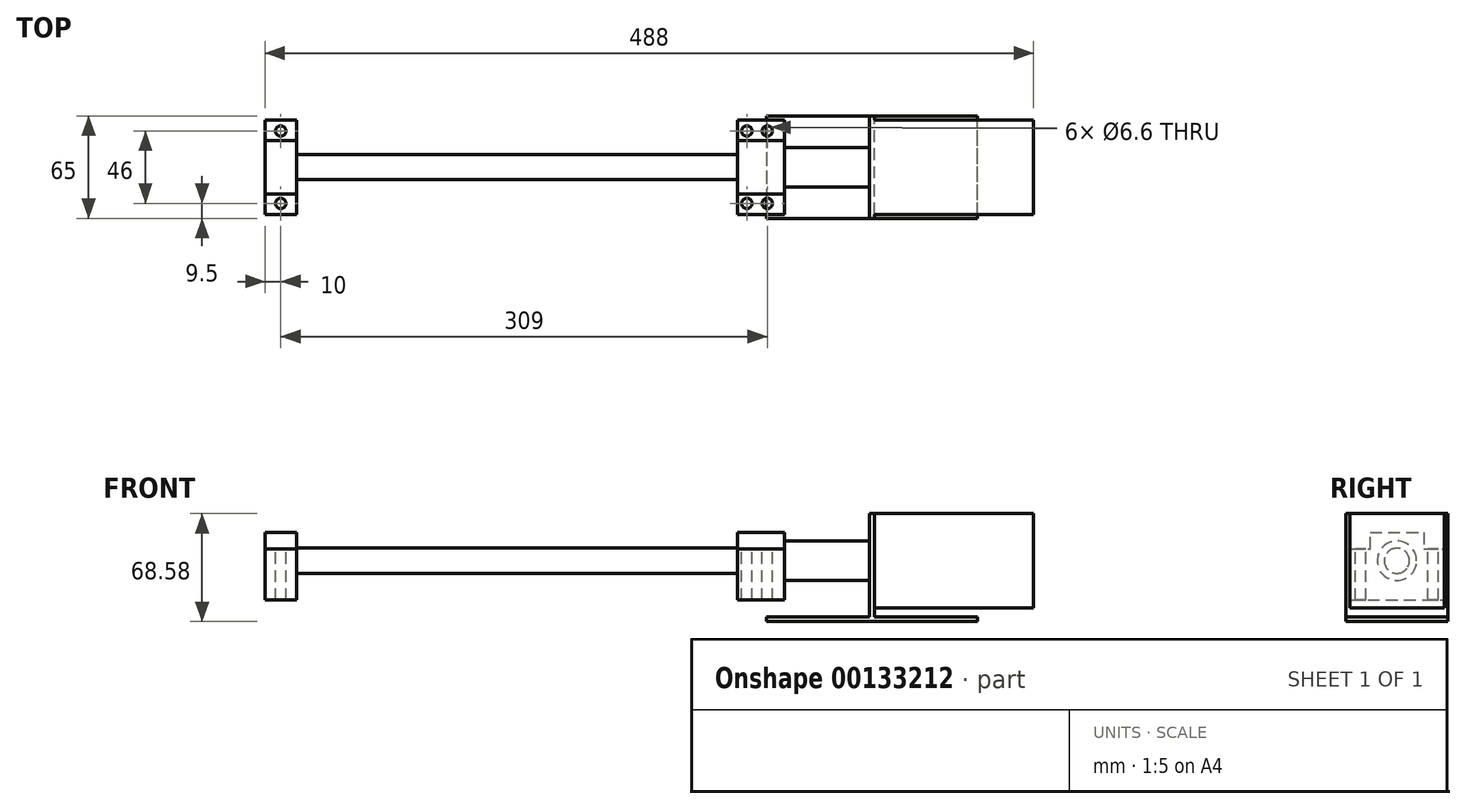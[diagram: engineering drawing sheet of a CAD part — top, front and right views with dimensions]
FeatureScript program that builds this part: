
annotation { "Feature Type Name" : "Feature", "Feature Type Description" : "" }
export const myFeature = defineFeature(function(context is Context, id is Id, definition is map)
    precondition{}
    {
        {
            var Q0;
            Q0=qCreatedBy(makeId("Right.planeOp"),FACE);
            var sketch = newSketch(context, id + "F0", { "sketchPlane" : qUnion([Q0])});
            skCircle(sketch, "E0", {"center": v(0, 0) * mm, "radius": 8 * mm});
            skSolve(sketch);
        }
        {
            var Q0;
            Q0=qSketchRegion(id+"F0",true);
            var Q1;
            Q1=qSketchRegion(id+"F2",true);
            extrude(context, id + "F1", {"entities" : qUnion([Q0, Q1]), "depth" : 330 * mm, "offsetDistance" : 25 * mm});
        }
        {
            var Q0;
            Q0=makeQuery(id+"F1.opExtrude","CAP_FACE",FACE,{"disambiguationData":[OSD([sQuery(id+"F0.wireOp",EDGE,"E0")])],"isStart":false});
            var sketch = newSketch(context, id + "F2", { "sketchPlane" : qUnion([Q0])});
            skLineSegment(sketch, "E1.bottom", {"start": v(17, 7.5) * mm, "end": v(30, 7.5) * mm});
            skLineSegment(sketch, "E1.top", {"start": v(-30, -25) * mm, "end": v(30, -25) * mm});
            skLineSegment(sketch, "E1.left", {"start": v(-30, 7.5) * mm, "end": v(-30, -25) * mm});
            skLineSegment(sketch, "E1.right", {"start": v(30, 7.5) * mm, "end": v(30, -25) * mm});
            skLineSegment(sketch, "E2", {"start": v(-17, 7.5) * mm, "end": v(-17, 18) * mm});
            skLineSegment(sketch, "E3", {"start": v(-17, 18) * mm, "end": v(17, 18) * mm});
            skLineSegment(sketch, "E4", {"start": v(17, 18) * mm, "end": v(17, 7.5) * mm});
            skLineSegment(sketch, "E5", {"start": v(-30, 7.5) * mm, "end": v(-17, 7.5) * mm});
            skSolve(sketch);
        }
        {
            var Q0;
            Q0=qSketchRegion(id+"F2",true);
            extrude(context, id + "F3", {"entities" : qUnion([Q0]), "operationType" : NewBodyOperationType.ADD, "oppositeDirection" : true, "depth" : (30) * mm, "offsetDistance" : 25 * mm});
        }
        {
            var Q0;
            Q0=makeQuery(id+"F1.opExtrude","CAP_FACE",FACE,{"disambiguationData":[OSD([sQuery(id+"F0.wireOp",EDGE,"E0")])],"isStart":true});
            var sketch = newSketch(context, id + "F4", { "sketchPlane" : qUnion([Q0])});
            skLineSegment(sketch, "E6.0", {"start": v(17, 18) * mm, "end": v(-17, 18) * mm});
            skLineSegment(sketch, "E7.0", {"start": v(-17, 18) * mm, "end": v(-17, 7.5) * mm});
            skLineSegment(sketch, "E8.0", {"start": v(-30, 7.5) * mm, "end": v(-30, -25) * mm});
            skLineSegment(sketch, "E9.0", {"start": v(30, -25) * mm, "end": v(-30, -25) * mm});
            skLineSegment(sketch, "E10.0", {"start": v(30, 7.5) * mm, "end": v(30, -25) * mm});
            skLineSegment(sketch, "E11.0", {"start": v(30, 7.5) * mm, "end": v(17, 7.5) * mm});
            skLineSegment(sketch, "E12.0", {"start": v(17, 7.5) * mm, "end": v(17, 18) * mm});
            skLineSegment(sketch, "E13", {"start": v(-30, 7.5) * mm, "end": v(-17, 7.5) * mm});
            skSolve(sketch);
        }
        {
            var Q0;
            Q0=qSketchRegion(id+"F4",true);
            extrude(context, id + "F5", {"entities" : qUnion([Q0]), "operationType" : NewBodyOperationType.ADD, "oppositeDirection" : true, "depth" : (20) * mm, "offsetDistance" : 25 * mm});
        }
        {
            var Q0;
            Q0=makeQuery(id+"F3.boolean.opBoolean","MERGE",FACE,{"derivedFrom":[makeQuery(id+"F1.opExtrude","CAP_FACE",FACE,{"disambiguationData":[OSD([sQuery(id+"F0.wireOp",EDGE,"E0")])],"isStart":false}),makeQuery(id+"F3.opExtrude","CAP_FACE",FACE,{"disambiguationData":[OSD([sQuery(id+"F2.wireOp",EDGE,"E1.bottom"),sQuery(id+"F2.wireOp",EDGE,"E1.top"),sQuery(id+"F2.wireOp",EDGE,"E1.left"),sQuery(id+"F2.wireOp",EDGE,"E1.right"),sQuery(id+"F2.wireOp",EDGE,"E2"),sQuery(id+"F2.wireOp",EDGE,"E3"),sQuery(id+"F2.wireOp",EDGE,"E4"),sQuery(id+"F2.wireOp",EDGE,"E5")])],"isStart":true})]});
            var sketch = newSketch(context, id + "F6", { "sketchPlane" : qUnion([Q0])});
            skCircle(sketch, "E14", {"center": v(0, 0) * mm, "radius": 12.5 * mm});
            skSolve(sketch);
        }
        {
            var Q0;
            Q0=qSketchRegion(id+"F6",true);
            extrude(context, id + "F7", {"entities" : qUnion([Q0]), "operationType" : NewBodyOperationType.ADD, "depth" : (57) * mm, "offsetDistance" : 25 * mm});
        }
        {
            var Q0;
            Q0=makeQuery(id+"F3.opExtrude","SWEPT_FACE",FACE,{"disambiguationData":[OSD([sQuery(id+"F2.wireOp",EDGE,"E3")])]});
            var sketch = newSketch(context, id + "F8", { "sketchPlane" : qUnion([Q0])});
            skCircle(sketch, "E15", {"center": v(306, 23) * mm, "radius": 3.3 * mm});
            skCircle(sketch, "E16", {"center": v(319, 23) * mm, "radius": 3.3 * mm});
            skCircle(sketch, "E17", {"center": v(306, -23) * mm, "radius": 3.3 * mm});
            skCircle(sketch, "E18", {"center": v(319, -23) * mm, "radius": 3.3 * mm});
            skCircle(sketch, "E19", {"center": v(10, 23) * mm, "radius": 3.3 * mm});
            skCircle(sketch, "E20", {"center": v(10, -23) * mm, "radius": 3.3 * mm});
            skSolve(sketch);
        }
        {
            var Q0;
            Q0=qSketchRegion(id+"F8",true);
            extrude(context, id + "F9", {"entities" : qUnion([Q0]), "operationType" : NewBodyOperationType.REMOVE, "endBound" : BoundingType.THROUGH_ALL, "oppositeDirection" : true, "depth" : 25 * mm, "offsetDistance" : 25 * mm});
        }
        {
            var Q0;
            Q0=makeQuery(id+"F7.opExtrude","CAP_FACE",FACE,{"disambiguationData":[OSD([sQuery(id+"F6.wireOp",EDGE,"E14")])],"isStart":false});
            var sketch = newSketch(context, id + "F10", { "sketchPlane" : qUnion([Q0])});
            skLineSegment(sketch, "E21.bottom", {"start": v(-30, 30) * mm, "end": v(30, 30) * mm});
            skLineSegment(sketch, "E21.top", {"start": v(-30, -30) * mm, "end": v(30, -30) * mm});
            skLineSegment(sketch, "E21.left", {"start": v(-30, 30) * mm, "end": v(-30, -30) * mm});
            skLineSegment(sketch, "E21.right", {"start": v(30, 30) * mm, "end": v(30, -30) * mm});
            skSolve(sketch);
        }
        {
            var Q0;
            Q0=qSketchRegion(id+"F10",true);
            extrude(context, id + "F11", {"entities" : qUnion([Q0]), "operationType" : NewBodyOperationType.ADD, "depth" : (101) * mm, "offsetDistance" : 25 * mm});
        }
        {
            var Q0;
            Q0=qCreatedBy(makeId("Front.planeOp"),FACE);
            var sketch = newSketch(context, id + "F12", { "sketchPlane" : qUnion([Q0])});
            skLineSegment(sketch, "E22.bottom", {"start": v(384, 30) * mm, "end": v(387, 30) * mm});
            skLineSegment(sketch, "E22.left", {"start": v(384, 30) * mm, "end": v(384, -38.58) * mm});
            skLineSegment(sketch, "E22.right", {"start": v(387, 30) * mm, "end": v(387, -35.58) * mm});
            skLineSegment(sketch, "E23.bottom", {"start": v(384, -38.58) * mm, "end": v(452.58, -38.58) * mm});
            skLineSegment(sketch, "E23.top", {"start": v(387, -35.58) * mm, "end": v(452.58, -35.58) * mm});
            skLineSegment(sketch, "E23.right", {"start": v(452.58, -38.58) * mm, "end": v(452.58, -35.58) * mm});
            skSolve(sketch);
        }
        {
            var Q0;
            Q0=qSketchRegion(id+"F12",true);
            extrude(context, id + "F13", {"entities" : qUnion([Q0]), "operationType" : NewBodyOperationType.ADD, "depth" : (65) * mm, "offsetDistance" : 25 * mm, "symmetric" : true});
        }
        {
            var Q0;
            Q0=makeQuery(id+"F13.opExtrude","CAP_FACE",FACE,{"disambiguationData":[OSD([sQuery(id+"F12.wireOp",EDGE,"E22.bottom"),sQuery(id+"F12.wireOp",EDGE,"E22.left"),sQuery(id+"F12.wireOp",EDGE,"E22.right"),sQuery(id+"F12.wireOp",EDGE,"E23.bottom"),sQuery(id+"F12.wireOp",EDGE,"E23.top"),sQuery(id+"F12.wireOp",EDGE,"E23.right")])],"isStart":false});
            var sketch = newSketch(context, id + "F14", { "sketchPlane" : qUnion([Q0])});
            skLineSegment(sketch, "E24.bottom", {"start": v(318.42, -35.58) * mm, "end": v(384, -35.58) * mm});
            skLineSegment(sketch, "E24.top", {"start": v(318.42, -38.58) * mm, "end": v(384, -38.58) * mm});
            skLineSegment(sketch, "E24.left", {"start": v(318.42, -35.58) * mm, "end": v(318.42, -38.58) * mm});
            skLineSegment(sketch, "E24.right", {"start": v(384, -35.58) * mm, "end": v(384, -38.58) * mm});
            skSolve(sketch);
        }
        {
            var Q0;
            Q0 = qSketchRegion(id + "F14", true);
            var Q1;
            Q1=makeQuery(id+"F13.opExtrude","CAP_FACE",FACE,{"disambiguationData":[OSD([sQuery(id+"F12.wireOp",EDGE,"E22.bottom"),sQuery(id+"F12.wireOp",EDGE,"E22.left"),sQuery(id+"F12.wireOp",EDGE,"E22.right"),sQuery(id+"F12.wireOp",EDGE,"E23.bottom"),sQuery(id+"F12.wireOp",EDGE,"E23.top"),sQuery(id+"F12.wireOp",EDGE,"E23.right")])],"isStart":true});
            extrude(context, id + "F15", {"entities" : qUnion([Q0]), "operationType" : NewBodyOperationType.ADD, "endBound" : BoundingType.UP_TO_SURFACE, "oppositeDirection" : true, "depth" : 25.4 * mm, "endBoundEntityFace" : qUnion([Q1]), "offsetDistance" : 25.4 * mm});
        }
    });
